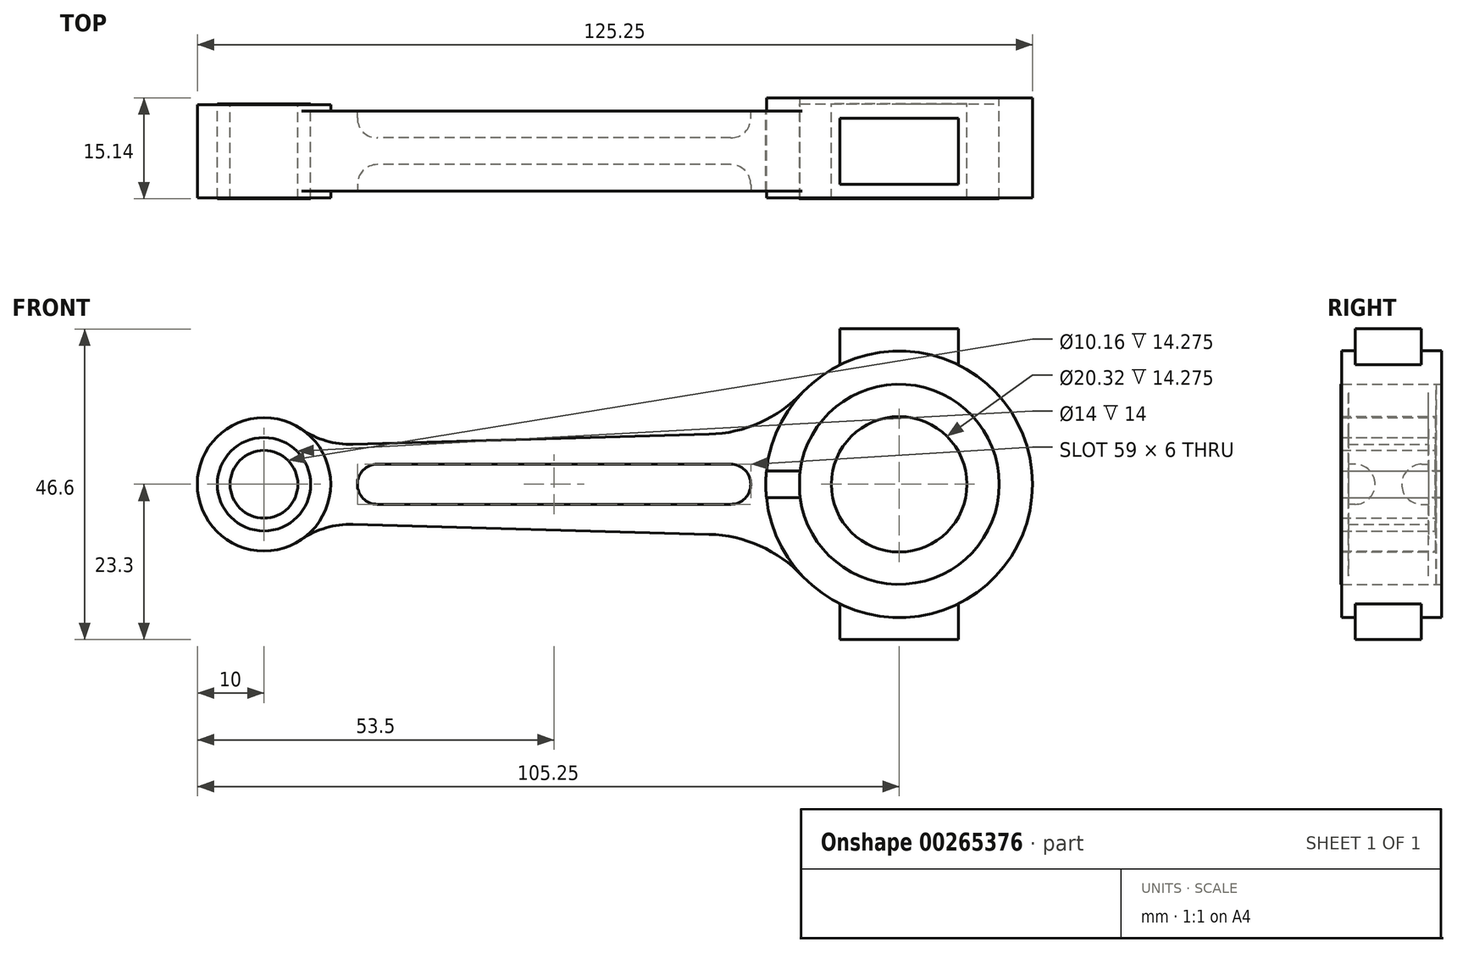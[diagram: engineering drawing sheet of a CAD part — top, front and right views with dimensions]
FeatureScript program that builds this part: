
annotation { "Feature Type Name" : "Feature", "Feature Type Description" : "" }
export const myFeature = defineFeature(function(context is Context, id is Id, definition is map)
    precondition{}
    {
        {
            var Q0;
            Q0=qCreatedBy(makeId("Front.planeOp"),FACE);
            var sketch = newSketch(context, id + "F0", { "sketchPlane" : qUnion([Q0])});
            skArc(sketch, "E0", {"start": v(9.8, 2) * mm, "mid": v(-10, 0) * mm, "end": v(9.8, -2) * mm});
            skCircle(sketch, "E1", {"center": v(0, 0) * mm, "radius": 7 * mm});
            skCircle(sketch, "E2", {"center": v(95.25, 0) * mm, "radius": 20 * mm});
            skCircle(sketch, "E3", {"center": v(95.25, 0) * mm, "radius": 15 * mm});
            skLineSegment(sketch, "E4", {"start": v(66.76, 7.5) * mm, "end": v(66.76, -7.5) * mm, "construction": true});
            skLineSegment(sketch, "E5", {"start": v(13.33, 6) * mm, "end": v(13.33, -6) * mm, "construction": true});
            skLineSegment(sketch, "E6", {"start": v(13.33, 6) * mm, "end": v(66.76, 7.5) * mm});
            skLineSegment(sketch, "E7", {"start": v(13.33, -6) * mm, "end": v(66.76, -7.5) * mm});
            skArc(sketch, "E8", {"start": v(13.33, -6) * mm, "mid": v(9.3, -6.52) * mm, "end": v(5.64, -8.26) * mm});
            skArc(sketch, "E9", {"start": v(80.72, -13.75) * mm, "mid": v(74.36, -9.23) * mm, "end": v(66.76, -7.5) * mm});
            skArc(sketch, "E10.MirrorCS", {"start": v(80.72, 13.75) * mm, "mid": v(74.36, 9.23) * mm, "end": v(66.76, 7.5) * mm});
            skArc(sketch, "E11.MirrorCS", {"start": v(13.33, 6) * mm, "mid": v(9.3, 6.52) * mm, "end": v(5.64, 8.26) * mm});
            skArc(sketch, "E12", {"start": v(17, 3) * mm, "mid": v(14, 0) * mm, "end": v(17, -3) * mm});
            skArc(sketch, "E13", {"start": v(70, -3) * mm, "mid": v(73, 0) * mm, "end": v(70, 3) * mm});
            skLineSegment(sketch, "E14", {"start": v(17, 3) * mm, "end": v(70, 3) * mm});
            skLineSegment(sketch, "E15", {"start": v(17, -3) * mm, "end": v(70, -3) * mm});
            skLineSegment(sketch, "E16", {"start": v(-21.36, 0) * mm, "end": v(128.45, 0) * mm, "construction": true});
            skLineSegment(sketch, "E17", {"start": v(75.35, 2) * mm, "end": v(80.38, 2) * mm});
            skLineSegment(sketch, "E18", {"start": v(75.35, -2) * mm, "end": v(80.38, -2) * mm});
            skCircle(sketch, "E19.0", {"center": v(95.25, 0) * mm, "radius": 17.5 * mm, "construction": true});
            skArc(sketch, "E20", {"start": v(12, -2) * mm, "mid": v(14, 0) * mm, "end": v(12, 2) * mm});
            skLineSegment(sketch, "E21", {"start": v(12, -2) * mm, "end": v(9.8, -2) * mm});
            skLineSegment(sketch, "E22.MirrorCS", {"start": v(12, 2) * mm, "end": v(9.8, 2) * mm});
            skSolve(sketch);
        }
        {
            var Q0;
            Q0=makeQuery(id+"F0.imprint","IMPRINT",FACE,{"disambiguationData":[TD([[makeQuery(id+"F0.imprint","IMPRINT",EDGE,{"derivedFrom":sQuery(id+"F0.wireOp",EDGE,"E13")}),1.0]])]});
            var Q1;
            Q1=makeQuery(id+"F0.imprint","IMPRINT",FACE,{"disambiguationData":[TD([[makeQuery(id+"F0.imprint","IMPRINT",EDGE,{"derivedFrom":sQuery(id+"F0.wireOp",EDGE,"E6")}),-1.0]])]});
            var Q2;
            {var subQ0=sQuery(id+"F0.wireOp",EDGE,"E17");Q2=makeQuery(id+"F0.imprint","IMPRINT",FACE,{"disambiguationData":[TD([[makeQuery(id+"F0.imprint","IMPRINT",EDGE,{"derivedFrom":subQ0}),1.0]])]});}
            var Q3;
            Q3=makeQuery(id+"F0.imprint","IMPRINT",FACE,{"disambiguationData":[TD([[makeQuery(id+"F0.imprint","IMPRINT",EDGE,{"derivedFrom":sQuery(id+"F0.wireOp",EDGE,"E1")}),-1.0]])]});
            extrude(context, id + "F1", {"entities" : qUnion([Q0, Q1, Q2, Q3]), "depth" : 12 * mm, "symmetric" : true});
        }
        {
            var Q0;
            Q0=makeQuery(id+"F1.opExtrude","CAP_FACE",FACE,{"disambiguationData":[OSD([sQuery(id+"F0.wireOp",EDGE,"E0"),sQuery(id+"F0.wireOp",EDGE,"E1"),sQuery(id+"F0.wireOp",EDGE,"E2"),sQuery(id+"F0.wireOp",EDGE,"E3"),sQuery(id+"F0.wireOp",EDGE,"E6"),sQuery(id+"F0.wireOp",EDGE,"E7"),sQuery(id+"F0.wireOp",EDGE,"E8"),sQuery(id+"F0.wireOp",EDGE,"E9"),sQuery(id+"F0.wireOp",EDGE,"E10.MirrorCS"),sQuery(id+"F0.wireOp",EDGE,"E11.MirrorCS"),sQuery(id+"F0.wireOp",EDGE,"E12"),sQuery(id+"F0.wireOp",EDGE,"E13"),sQuery(id+"F0.wireOp",EDGE,"E14"),sQuery(id+"F0.wireOp",EDGE,"E15"),sQuery(id+"F0.wireOp",EDGE,"E17"),sQuery(id+"F0.wireOp",EDGE,"E18")])],"isStart":true});
            var sketch = newSketch(context, id + "F2", { "sketchPlane" : qUnion([Q0])});
            skArc(sketch, "E23.0", {"start": v(-80.72, -13.75) * mm, "mid": v(-115.25, 0) * mm, "end": v(-80.72, 13.75) * mm});
            skArc(sketch, "E24.0", {"start": v(-80.38, -2) * mm, "mid": v(-110.25, 0) * mm, "end": v(-80.38, 2) * mm});
            skArc(sketch, "E25", {"start": v(-80.72, -13.75) * mm, "mid": v(-75.25, 0) * mm, "end": v(-80.72, 13.75) * mm});
            skCircle(sketch, "E26.0", {"center": v(0, 0) * mm, "radius": 7 * mm});
            skArc(sketch, "E27.0", {"start": v(-5.64, 8.26) * mm, "mid": v(10, 0) * mm, "end": v(-5.64, -8.26) * mm});
            skArc(sketch, "E28", {"start": v(-5.64, 8.26) * mm, "mid": v(-10, 0) * mm, "end": v(-5.64, -8.26) * mm});
            skLineSegment(sketch, "E29.0", {"start": v(-17, -3) * mm, "end": v(-70, -3) * mm});
            skLineSegment(sketch, "E30.0", {"start": v(-17, 3) * mm, "end": v(-70, 3) * mm});
            skArc(sketch, "E31.0", {"start": v(-70, -3) * mm, "mid": v(-73, 0) * mm, "end": v(-70, 3) * mm});
            skArc(sketch, "E32.0", {"start": v(-17, 3) * mm, "mid": v(-14, 0) * mm, "end": v(-17, -3) * mm});
            skLineSegment(sketch, "E33.0", {"start": v(-12, -2) * mm, "end": v(-9.8, -2) * mm});
            skArc(sketch, "E34.0", {"start": v(-12, -2) * mm, "mid": v(-14, 0) * mm, "end": v(-12, 2) * mm});
            skLineSegment(sketch, "E35.0", {"start": v(-12, 2) * mm, "end": v(-9.8, 2) * mm});
            skSolve(sketch);
        }
        {
            var Q0;
            {var subQ1=sQuery(id+"F2.wireOp",EDGE,"E23.0");Q0=makeQuery(id+"F2.imprint","IMPRINT",FACE,{"disambiguationData":[TD([[makeQuery(id+"F2.imprint","IMPRINT",EDGE,{"derivedFrom":subQ1}),-1.0]])]});}
            extrude(context, id + "F3", {"entities" : qUnion([Q0]), "operationType" : NewBodyOperationType.ADD, "depth" : 1 * mm});
        }
        {
            var Q0;
            Q0=makeQuery(id+"F2.imprint","IMPRINT",FACE,{"disambiguationData":[TD([[makeQuery(id+"F2.imprint","IMPRINT",EDGE,{"derivedFrom":sQuery(id+"F2.wireOp",EDGE,"E26.0")}),1.0]])]});
            var Q1;
            Q1=makeQuery(id+"F3.opExtrude","CAP_FACE",FACE,{"disambiguationData":[OSD([sQuery(id+"F0.wireOp",EDGE,"E17"),sQuery(id+"F0.wireOp",EDGE,"E18"),sQuery(id+"F2.wireOp",EDGE,"E23.0"),sQuery(id+"F2.wireOp",EDGE,"E24.0"),sQuery(id+"F2.wireOp",EDGE,"E25")])],"isStart":false});
            extrude(context, id + "F4", {"entities" : qUnion([Q0, Q1]), "operationType" : NewBodyOperationType.ADD, "depth" : 1 * mm});
        }
        {
            var Q0;
            {var subQ3=sQuery(id+"F2.wireOp",EDGE,"E29.0");Q0=makeQuery(id+"F2.imprint","IMPRINT",FACE,{"disambiguationData":[TD([[makeQuery(id+"F2.imprint","IMPRINT",EDGE,{"derivedFrom":subQ3}),-1.0]])]});}
            extrude(context, id + "F5", {"entities" : qUnion([Q0]), "operationType" : NewBodyOperationType.REMOVE, "oppositeDirection" : true, "depth" : 4 * mm});
        }
        {
            var Q0;
            Q0=makeQuery(id+"F1.opExtrude","CAP_FACE",FACE,{"disambiguationData":[OSD([sQuery(id+"F0.wireOp",EDGE,"E0"),sQuery(id+"F0.wireOp",EDGE,"E1"),sQuery(id+"F0.wireOp",EDGE,"E2"),sQuery(id+"F0.wireOp",EDGE,"E3"),sQuery(id+"F0.wireOp",EDGE,"E6"),sQuery(id+"F0.wireOp",EDGE,"E7"),sQuery(id+"F0.wireOp",EDGE,"E8"),sQuery(id+"F0.wireOp",EDGE,"E9"),sQuery(id+"F0.wireOp",EDGE,"E10.MirrorCS"),sQuery(id+"F0.wireOp",EDGE,"E11.MirrorCS"),sQuery(id+"F0.wireOp",EDGE,"E17"),sQuery(id+"F0.wireOp",EDGE,"E18")])],"isStart":false});
            var sketch = newSketch(context, id + "F6", { "sketchPlane" : qUnion([Q0])});
            skArc(sketch, "E36.0.0", {"start": v(13.33, 6) * mm, "mid": v(9.3, 6.52) * mm, "end": v(5.64, 8.26) * mm});
            skArc(sketch, "E36.0.1", {"start": v(5.64, 8.26) * mm, "mid": v(-10, 0) * mm, "end": v(5.64, -8.26) * mm});
            skArc(sketch, "E36.0.2", {"start": v(5.64, -8.26) * mm, "mid": v(9.3, -6.52) * mm, "end": v(13.33, -6) * mm});
            skLineSegment(sketch, "E36.0.3", {"start": v(13.33, -6) * mm, "end": v(66.76, -7.5) * mm});
            skArc(sketch, "E36.0.4", {"start": v(66.76, -7.5) * mm, "mid": v(74.36, -9.23) * mm, "end": v(80.72, -13.75) * mm});
            skArc(sketch, "E36.0.5", {"start": v(80.72, -13.75) * mm, "mid": v(115.25, 0) * mm, "end": v(80.72, 13.75) * mm});
            skArc(sketch, "E36.0.6", {"start": v(80.72, 13.75) * mm, "mid": v(74.36, 9.23) * mm, "end": v(66.76, 7.5) * mm});
            skLineSegment(sketch, "E36.0.7", {"start": v(66.76, 7.5) * mm, "end": v(13.33, 6) * mm});
            skArc(sketch, "E37.0", {"start": v(80.72, -13.75) * mm, "mid": v(75.25, 0) * mm, "end": v(80.72, 13.75) * mm});
            skLineSegment(sketch, "E38.0", {"start": v(17, 3) * mm, "end": v(70, 3) * mm});
            skLineSegment(sketch, "E39.0", {"start": v(17, -3) * mm, "end": v(70, -3) * mm});
            skArc(sketch, "E40.0", {"start": v(70, -3) * mm, "mid": v(73, 0) * mm, "end": v(70, 3) * mm});
            skArc(sketch, "E41.0", {"start": v(17, 3) * mm, "mid": v(14, 0) * mm, "end": v(17, -3) * mm});
            skArc(sketch, "E42.0", {"start": v(5.64, 8.26) * mm, "mid": v(10, 0) * mm, "end": v(5.64, -8.26) * mm});
            skSolve(sketch);
        }
        {
            var Q0;
            Q0=makeQuery(id+"F6.imprint","IMPRINT",FACE,{"disambiguationData":[TD([[makeQuery(id+"F6.imprint","IMPRINT",EDGE,{"derivedFrom":sQuery(id+"F6.wireOp",EDGE,"E38.0")}),-1.0]])]});
            extrude(context, id + "F7", {"entities" : qUnion([Q0]), "operationType" : NewBodyOperationType.REMOVE, "oppositeDirection" : true, "depth" : 4 * mm});
        }
        {
            var Q0;
            {var subQ1=sQuery(id+"F6.wireOp",EDGE,"E36.0.5");Q0=makeQuery(id+"F6.imprint","IMPRINT",FACE,{"disambiguationData":[TD([[makeQuery(id+"F6.imprint","IMPRINT",EDGE,{"derivedFrom":subQ1}),1.0]])]});}
            var Q1;
            Q1=makeQuery(id+"F6.imprint","IMPRINT",FACE,{"disambiguationData":[TD([[makeQuery(id+"F6.imprint","IMPRINT",EDGE,{"derivedFrom":sQuery(id+"F6.wireOp",EDGE,"E36.0.1")}),1.0]])]});
            extrude(context, id + "F8", {"entities" : qUnion([Q0, Q1]), "operationType" : NewBodyOperationType.ADD, "depth" : 1 * mm});
        }
        {
            var Q0;
            Q0=makeQuery(id+"F5.boolean.opBoolean","COPY",EDGE,{"derivedFrom":makeQuery(id+"F5.opExtrude","CAP_EDGE",EDGE,{"disambiguationData":[OSD([sQuery(id+"F2.wireOp",EDGE,"E30.0")])],"isStart":false})});
            fillet(context, id + "F9", {"entities" : qUnion([Q0]), "radius" : 3 * mm, "tangentPropagation" : true, "allowEdgeOverflow" : false});
        }
        {
            var Q0;
            Q0=makeQuery(id+"F7.boolean.opBoolean","COPY",FACE,{"derivedFrom":makeQuery(id+"F7.opExtrude","CAP_FACE",FACE,{"disambiguationData":[OSD([sQuery(id+"F6.wireOp",EDGE,"E38.0"),sQuery(id+"F6.wireOp",EDGE,"E39.0"),sQuery(id+"F6.wireOp",EDGE,"E40.0"),sQuery(id+"F6.wireOp",EDGE,"E41.0")])],"isStart":false})});
            fillet(context, id + "F10", {"entities" : qUnion([Q0]), "radius" : 3 * mm, "tangentPropagation" : true, "allowEdgeOverflow" : false});
        }
        {
            var Q0;
            Q0=qCreatedBy(makeId("Front.planeOp"),FACE);
            var sketch = newSketch(context, id + "F11", { "sketchPlane" : qUnion([Q0])});
            skArc(sketch, "E43.0", {"start": v(80.38, -2) * mm, "mid": v(110.25, 0) * mm, "end": v(80.38, 2) * mm});
            skArc(sketch, "E44.0", {"start": v(75.35, 2) * mm, "mid": v(112.75, 9.68) * mm, "end": v(86.36, -17.92) * mm});
            skLineSegment(sketch, "E45", {"start": v(95.25, 20) * mm, "end": v(95.25, 23.3) * mm});
            skLineSegment(sketch, "E46", {"start": v(95.25, 23.3) * mm, "end": v(104.14, 23.3) * mm});
            skLineSegment(sketch, "E47", {"start": v(104.14, 23.3) * mm, "end": v(104.14, 17.92) * mm});
            skLineSegment(sketch, "E48", {"start": v(95.25, 23.3) * mm, "end": v(86.36, 23.3) * mm});
            skLineSegment(sketch, "E49", {"start": v(86.36, 23.3) * mm, "end": v(86.36, 17.92) * mm});
            skArc(sketch, "E50.0.0", {"start": v(75.35, -2) * mm, "mid": v(85.57, -17.5) * mm, "end": v(104.14, -17.92) * mm});
            skLineSegment(sketch, "E50.0.1", {"start": v(75.35, 2) * mm, "end": v(80.38, 2) * mm});
            skArc(sketch, "E50.0.2", {"start": v(80.38, 2) * mm, "mid": v(110.25, 0) * mm, "end": v(80.38, -2) * mm});
            skLineSegment(sketch, "E50.0.3", {"start": v(80.38, -2) * mm, "end": v(75.35, -2) * mm});
            skLineSegment(sketch, "E51.MirrorCS", {"start": v(86.36, -23.3) * mm, "end": v(86.36, -17.92) * mm});
            skLineSegment(sketch, "E52.MirrorCS", {"start": v(95.25, -23.3) * mm, "end": v(86.36, -23.3) * mm});
            skLineSegment(sketch, "E53.MirrorCS", {"start": v(95.25, -20) * mm, "end": v(95.25, -23.3) * mm});
            skLineSegment(sketch, "E54.MirrorCS", {"start": v(95.25, -23.3) * mm, "end": v(104.14, -23.3) * mm});
            skLineSegment(sketch, "E55.MirrorCS", {"start": v(104.14, -23.3) * mm, "end": v(104.14, -17.92) * mm});
            skArc(sketch, "E56.MirrorCS", {"start": v(75.35, 2) * mm, "mid": v(115.25, 0) * mm, "end": v(75.35, -2) * mm});
            skArc(sketch, "E57.trimOffspring", {"start": v(104.14, 17.92) * mm, "mid": v(95.25, 20) * mm, "end": v(86.36, 17.92) * mm});
            skSolve(sketch);
        }
        {
            var Q0;
            {var subQ0=sQuery(id+"F11.wireOp",EDGE,"E45");Q0=makeQuery(id+"F11.imprint","IMPRINT",FACE,{"disambiguationData":[TD([[makeQuery(id+"F11.imprint","IMPRINT",EDGE,{"derivedFrom":subQ0}),-1.0]])]});}
            var Q1;
            {var subQ0=sQuery(id+"F11.wireOp",EDGE,"E45");Q1=makeQuery(id+"F11.imprint","IMPRINT",FACE,{"disambiguationData":[TD([[makeQuery(id+"F11.imprint","IMPRINT",EDGE,{"derivedFrom":subQ0}),1.0]])]});}
            var Q2;
            {var subQ0=sQuery(id+"F11.wireOp",EDGE,"E53.MirrorCS");Q2=makeQuery(id+"F11.imprint","IMPRINT",FACE,{"disambiguationData":[TD([[makeQuery(id+"F11.imprint","IMPRINT",EDGE,{"derivedFrom":subQ0}),1.0]])]});}
            var Q3;
            {var subQ0=sQuery(id+"F11.wireOp",EDGE,"E51.MirrorCS");Q3=makeQuery(id+"F11.imprint","IMPRINT",FACE,{"disambiguationData":[TD([[makeQuery(id+"F11.imprint","IMPRINT",EDGE,{"derivedFrom":subQ0}),-1.0]])]});}
            extrude(context, id + "F12", {"entities" : qUnion([Q0, Q1, Q2, Q3]), "operationType" : NewBodyOperationType.ADD, "depth" : 9.9 * mm, "symmetric" : true});
        }
        {
            var Q0;
            Q0=qCreatedBy(makeId("Front.planeOp"),FACE);
            var sketch = newSketch(context, id + "F13", { "sketchPlane" : qUnion([Q0])});
            skCircle(sketch, "E58.0", {"center": v(0, 0) * mm, "radius": 7 * mm});
            skArc(sketch, "E59.0", {"start": v(80.38, -2) * mm, "mid": v(110.25, 0) * mm, "end": v(80.38, 2) * mm});
            skCircle(sketch, "E60", {"center": v(0, 0) * mm, "radius": 5.08 * mm});
            skCircle(sketch, "E61", {"center": v(95.25, 0) * mm, "radius": 10.16 * mm});
            skArc(sketch, "E62", {"start": v(80.38, 2) * mm, "mid": v(80.32, 0) * mm, "end": v(80.38, -2) * mm});
            skSolve(sketch);
        }
        {
            var Q0;
            Q0=makeQuery(id+"F13.imprint","IMPRINT",FACE,{"disambiguationData":[TD([[makeQuery(id+"F13.imprint","IMPRINT",EDGE,{"derivedFrom":sQuery(id+"F13.wireOp",EDGE,"E59.0")}),1.0]])]});
            var Q1;
            Q1=makeQuery(id+"F13.imprint","IMPRINT",FACE,{"disambiguationData":[TD([[makeQuery(id+"F13.imprint","IMPRINT",EDGE,{"derivedFrom":sQuery(id+"F13.wireOp",EDGE,"E58.0")}),1.0]])]});
            extrude(context, id + "F14", {"entities" : qUnion([Q0, Q1]), "depth" : 14.27 * mm, "symmetric" : true});
        }
    });
